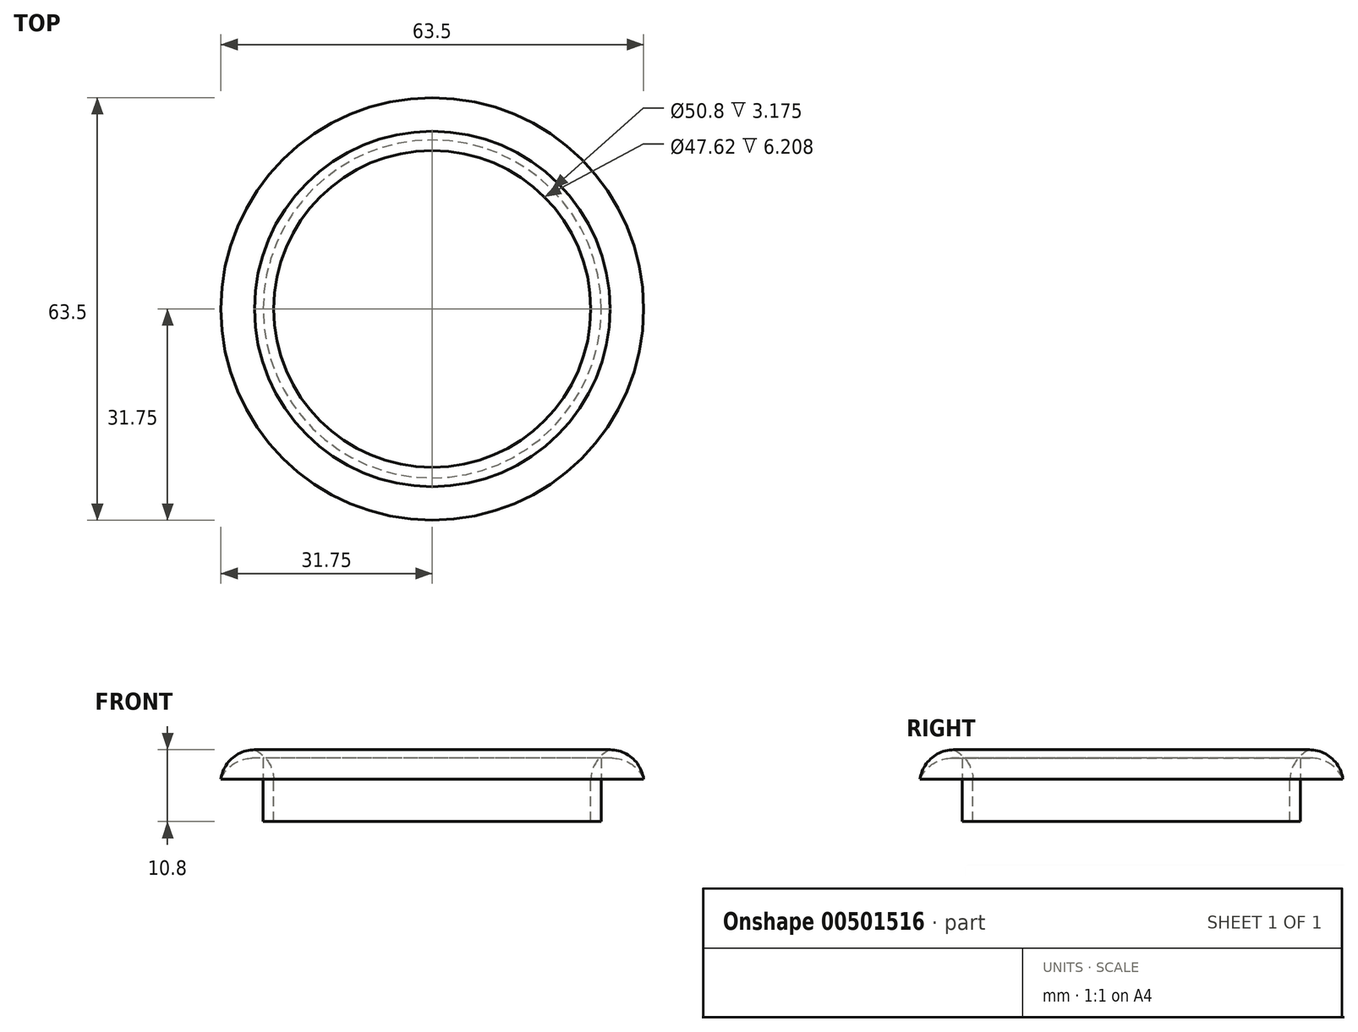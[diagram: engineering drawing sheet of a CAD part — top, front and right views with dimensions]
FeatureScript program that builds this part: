
annotation { "Feature Type Name" : "Feature", "Feature Type Description" : "" }
export const myFeature = defineFeature(function(context is Context, id is Id, definition is map)
    precondition{}
    {
        {
            var Q0;
            Q0=qCreatedBy(makeId("Top.planeOp"),FACE);
            var sketch = newSketch(context, id + "F0", { "sketchPlane" : qUnion([Q0])});
            skCircle(sketch, "E0", {"center": v(0, 0) * mm, "radius": 25.4 * mm});
            skCircle(sketch, "E1", {"center": v(0, 0) * mm, "radius": 23.81 * mm});
            skCircle(sketch, "E2", {"center": v(0, 0) * mm, "radius": 31.75 * mm});
            skSolve(sketch);
        }
        {
            var Q0;
            Q0=makeQuery(id+"F0.imprint","IMPRINT",FACE,{"disambiguationData":[TD([[makeQuery(id+"F0.imprint","IMPRINT",EDGE,{"derivedFrom":sQuery(id+"F0.wireOp",EDGE,"E0")}),1.0]])]});
            extrude(context, id + "F1", {"entities" : qUnion([Q0]), "oppositeDirection" : true, "depth" : 6.35 * mm});
        }
        {
            var Q0;
            Q0=makeQuery(id+"F0.imprint","IMPRINT",FACE,{"disambiguationData":[TD([[makeQuery(id+"F0.imprint","IMPRINT",EDGE,{"derivedFrom":sQuery(id+"F0.wireOp",EDGE,"E0")}),-1.0]])]});
            var Q1;
            Q1=makeQuery(id+"F0.imprint","IMPRINT",FACE,{"disambiguationData":[TD([[makeQuery(id+"F0.imprint","IMPRINT",EDGE,{"derivedFrom":sQuery(id+"F0.wireOp",EDGE,"E0")}),1.0]])]});
            extrude(context, id + "F2", {"entities" : qUnion([Q0, Q1]), "operationType" : NewBodyOperationType.ADD, "depth" : 4.44 * mm});
        }
        {
            var Q0;
            Q0=makeQuery(id+"F2.opExtrude","CAP_EDGE",EDGE,{"disambiguationData":[OSD([sQuery(id+"F0.wireOp",EDGE,"E2")])],"isStart":false});
            fillet(context, id + "F3", {"entities" : qUnion([Q0]), "radius" : 5.08 * mm, "tangentPropagation" : true, "allowEdgeOverflow" : false});
        }
        {
            var Q0;
            Q0=makeQuery(id+"F2.opExtrude","CAP_EDGE",EDGE,{"disambiguationData":[OSD([sQuery(id+"F0.wireOp",EDGE,"E1")])],"isStart":false});
            fillet(context, id + "F4", {"entities" : qUnion([Q0]), "radius" : 5.08 * mm, "tangentPropagation" : true, "allowEdgeOverflow" : false});
        }
        {
            var Q0;
            Q0=makeQuery(id+"F0.imprint","IMPRINT",FACE,{"disambiguationData":[TD([[makeQuery(id+"F0.imprint","IMPRINT",EDGE,{"derivedFrom":sQuery(id+"F0.wireOp",EDGE,"E0")}),-1.0]])]});
            extrude(context, id + "F5", {"entities" : qUnion([Q0]), "depth" : 3.17 * mm});
        }
        {
            var Q0;
            Q0=makeQuery(id+"F5.opExtrude","CAP_EDGE",EDGE,{"disambiguationData":[OSD([sQuery(id+"F0.wireOp",EDGE,"E2")])],"isStart":false});
            fillet(context, id + "F6", {"entities" : qUnion([Q0]), "radius" : 5.08 * mm, "tangentPropagation" : true, "allowEdgeOverflow" : false});
        }
    });
